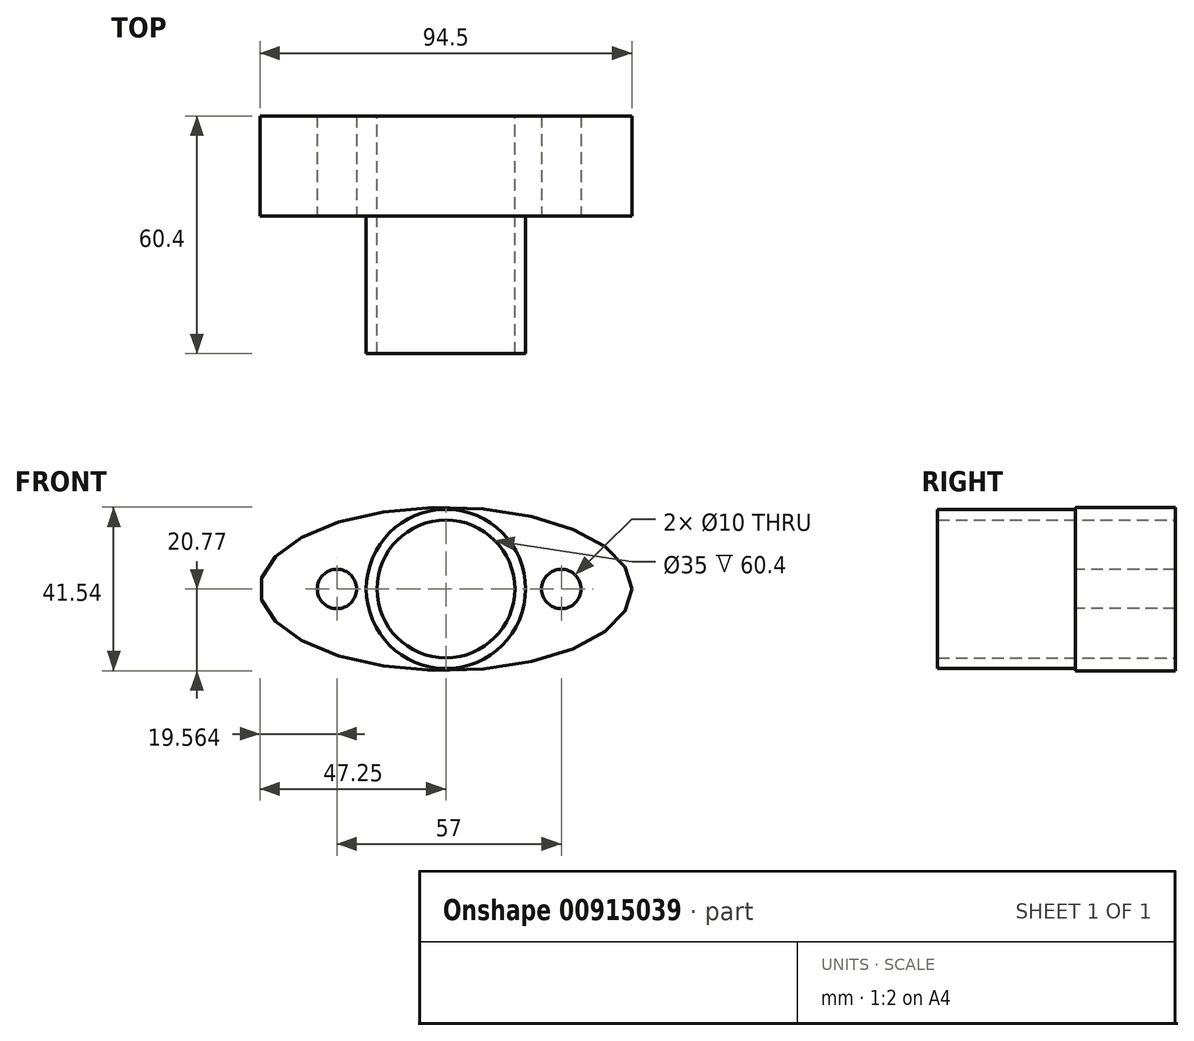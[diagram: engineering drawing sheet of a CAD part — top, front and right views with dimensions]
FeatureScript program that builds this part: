
annotation { "Feature Type Name" : "Feature", "Feature Type Description" : "" }
export const myFeature = defineFeature(function(context is Context, id is Id, definition is map)
    precondition{}
    {
        {
            var Q0;
            Q0=qCreatedBy(makeId("Front.planeOp"),FACE);
            var sketch = newSketch(context, id + "F0", { "sketchPlane" : qUnion([Q0])});
            skEllipse(sketch, "E0", {"center": v(0, 0) * mm, "majorRadius": 47.25 * mm, "minorRadius": 20.77 * mm, "majorAxis": v(1, 0)});
            skCircle(sketch, "E1", {"center": v(0, 0) * mm, "radius": 17.5 * mm});
            skSolve(sketch);
        }
        {
            var Q0;
            Q0 = qSketchRegion(id + "F0", true);
            extrude(context, id + "F1", {"entities" : qUnion([Q0]), "depth" : 25.4 * mm, "offsetDistance" : 25.4 * mm});
        }
        {
            var Q0;
            Q0=makeQuery(id+"F1.opExtrude","CAP_FACE",FACE,{"disambiguationData":[OSD([sQuery(id+"F0.wireOp",EDGE,"E0"),sQuery(id+"F0.wireOp",EDGE,"E1")])],"isStart":false});
            var sketch = newSketch(context, id + "F2", { "sketchPlane" : qUnion([Q0])});
            skSolve(sketch);
        }
        {
            var Q0;
            Q0=makeQuery(id+"F2.imprint","IMPRINT",FACE,{"disambiguationData":[TD([[makeQuery(id+"F2.imprint","IMPRINT",EDGE,{"derivedFrom":makeQuery(id+"F1.opExtrude","CAP_EDGE",EDGE,{"disambiguationData":[OSD([sQuery(id+"F0.wireOp",EDGE,"E0")])],"isStart":false})}),1.0]])]});
            var sketch = newSketch(context, id + "F3", { "sketchPlane" : qUnion([Q0])});
            skCircle(sketch, "E2", {"center": v(0, 0) * mm, "radius": 20.25 * mm});
            skCircle(sketch, "E3", {"center": v(0, 0) * mm, "radius": 17.5 * mm});
            skSolve(sketch);
        }
        {
            var Q0;
            Q0 = qSketchRegion(id + "F3", true);
            extrude(context, id + "F4", {"entities" : qUnion([Q0]), "operationType" : NewBodyOperationType.ADD, "depth" : 35 * mm, "offsetDistance" : 25.4 * mm});
        }
        {
            var Q0;
            Q0=makeQuery(id+"F2.imprint","IMPRINT",FACE,{"disambiguationData":[TD([[makeQuery(id+"F2.imprint","IMPRINT",EDGE,{"derivedFrom":makeQuery(id+"F1.opExtrude","CAP_EDGE",EDGE,{"disambiguationData":[OSD([sQuery(id+"F0.wireOp",EDGE,"E0")])],"isStart":false})}),1.0]])]});
            var sketch = newSketch(context, id + "F5", { "sketchPlane" : qUnion([Q0])});
            skPoint(sketch, "E4", {"position": v(-27.69, 0) * mm});
            skPoint(sketch, "E5", {"position": v(29.31, 0) * mm});
            skSolve(sketch);
        }
        {
            var Q0;
            Q0=sQuery(id+"F5.wireOp",VERTEX,"E4");
            var Q1;
            Q1=sQuery(id+"F5.wireOp",VERTEX,"E5");
            var Q2;
            Q2=makeQuery(id+"F1.opExtrude","SWEPT_BODY",BODY,{"disambiguationData":[OSD([sQuery(id+"F0.wireOp",EDGE,"E0"),sQuery(id+"F0.wireOp",EDGE,"E1")])]});
            hole(context, id + "F6", {"style" : HoleStyle.SIMPLE, "endStyle" : HoleEndStyle.THROUGH, "holeDiameter" : 10 * mm, "majorDiameter" : 6.35 * mm, "isTappedThrough" : true, "tappedDepth" : 12.7 * mm, "tapClearance" : 3, "locations" : qUnion([Q0, Q1]), "scope" : qUnion([Q2])});
        }
    });
